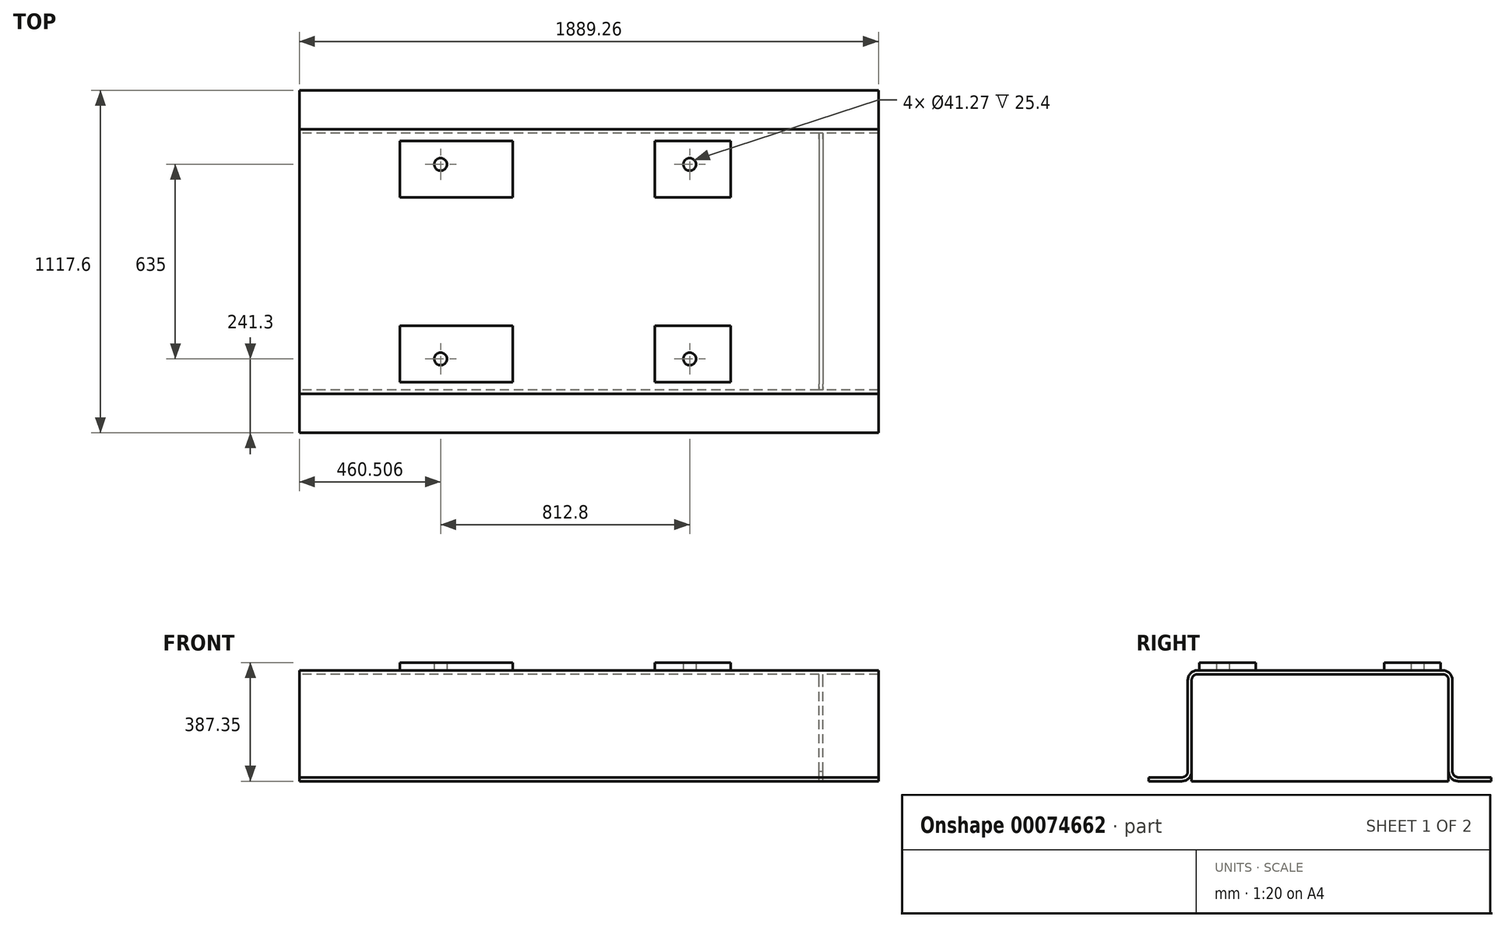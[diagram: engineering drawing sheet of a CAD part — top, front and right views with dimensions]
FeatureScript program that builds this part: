
annotation { "Feature Type Name" : "Feature", "Feature Type Description" : "" }
export const myFeature = defineFeature(function(context is Context, id is Id, definition is map)
    precondition{}
    {
        {
            var Q0;
            Q0=qCreatedBy(makeId("Right.planeOp"),FACE);
            var sketch = newSketch(context, id + "F0", { "sketchPlane" : qUnion([Q0])});
            skLineSegment(sketch, "E0", {"start": v(-558.8, 0) * mm, "end": v(558.8, 0) * mm, "construction": true});
            skLineSegment(sketch, "E1.0", {"start": v(-558.8, 361.95) * mm, "end": v(558.8, 361.95) * mm, "construction": true});
            skLineSegment(sketch, "E2.bottom", {"start": v(0, 361.95) * mm, "end": v(400.05, 361.95) * mm});
            skLineSegment(sketch, "E2.top", {"start": v(450.85, 0) * mm, "end": v(558.8, 0) * mm});
            skLineSegment(sketch, "E2.right", {"start": v(558.8, 12.7) * mm, "end": v(558.8, 0) * mm});
            skLineSegment(sketch, "E3.0", {"start": v(0, 349.25) * mm, "end": v(400.05, 349.25) * mm});
            skLineSegment(sketch, "E4.0", {"start": v(450.85, 12.7) * mm, "end": v(558.8, 12.7) * mm});
            skLineSegment(sketch, "E5", {"start": v(0, -75.24) * mm, "end": v(0, 457.7) * mm, "construction": true});
            skLineSegment(sketch, "E6.0", {"start": v(431.8, 31.75) * mm, "end": v(431.8, 330.2) * mm});
            skLineSegment(sketch, "E7.0", {"start": v(419.1, 31.75) * mm, "end": v(419.1, 330.2) * mm});
            skArc(sketch, "E8.filletArc", {"start": v(419.1, 330.2) * mm, "mid": v(413.52, 343.67) * mm, "end": v(400.05, 349.25) * mm});
            skArc(sketch, "E9.filletArc", {"start": v(431.8, 31.75) * mm, "mid": v(437.38, 18.28) * mm, "end": v(450.85, 12.7) * mm});
            skArc(sketch, "E10.filletArc", {"start": v(431.8, 330.2) * mm, "mid": v(422.5, 352.65) * mm, "end": v(400.05, 361.95) * mm});
            skArc(sketch, "E11.filletArc", {"start": v(419.1, 31.75) * mm, "mid": v(428.4, 9.3) * mm, "end": v(450.85, 0) * mm});
            skLineSegment(sketch, "E12.0", {"start": v(450.85, 6.35) * mm, "end": v(558.8, 6.35) * mm});
            skArc(sketch, "E13.MirrorCS", {"start": v(-419.1, 330.2) * mm, "mid": v(-413.52, 343.67) * mm, "end": v(-400.05, 349.25) * mm});
            skLineSegment(sketch, "E14.MirrorCS", {"start": v(-558.8, 12.7) * mm, "end": v(-558.8, 0) * mm});
            skArc(sketch, "E15.MirrorCS", {"start": v(-431.8, 31.75) * mm, "mid": v(-437.38, 18.28) * mm, "end": v(-450.85, 12.7) * mm});
            skLineSegment(sketch, "E16.MirrorCS", {"start": v(-450.85, 6.35) * mm, "end": v(-558.8, 6.35) * mm});
            skLineSegment(sketch, "E17.MirrorCS", {"start": v(-450.85, 12.7) * mm, "end": v(-558.8, 12.7) * mm});
            skLineSegment(sketch, "E18.MirrorCS", {"start": v(-450.85, 0) * mm, "end": v(-558.8, 0) * mm});
            skArc(sketch, "E19.MirrorCS", {"start": v(-419.1, 31.75) * mm, "mid": v(-428.4, 9.3) * mm, "end": v(-450.85, 0) * mm});
            skArc(sketch, "E20.MirrorCS", {"start": v(-431.8, 330.2) * mm, "mid": v(-422.5, 352.65) * mm, "end": v(-400.05, 361.95) * mm});
            skLineSegment(sketch, "E21.MirrorCS", {"start": v(-431.8, 31.75) * mm, "end": v(-431.8, 330.2) * mm});
            skLineSegment(sketch, "E22.MirrorCS", {"start": v(0, 349.25) * mm, "end": v(-400.05, 349.25) * mm});
            skLineSegment(sketch, "E23.MirrorCS", {"start": v(-419.1, 31.75) * mm, "end": v(-419.1, 330.2) * mm});
            skLineSegment(sketch, "E24.MirrorCS", {"start": v(0, 361.95) * mm, "end": v(-400.05, 361.95) * mm});
            skSolve(sketch);
        }
        {
            var Q0;
            Q0 = qSketchRegion(id + "F0", true);
            extrude(context, id + "F1", {"entities" : qUnion([Q0]), "endBound" : BoundingType.SYMMETRIC, "depth" : 1889.25 * mm});
        }
        {
            var Q0;
            Q0=makeQuery(id+"F1.opExtrude","SWEPT_FACE",FACE,{"disambiguationData":[OSD([sQuery(id+"F0.wireOp",EDGE,"E3.0"),sQuery(id+"F0.wireOp",EDGE,"E22.MirrorCS")])]});
            var sketch = newSketch(context, id + "F2", { "sketchPlane" : qUnion([Q0])});
            skLineSegment(sketch, "E25.0", {"start": v(763.78, 419.1) * mm, "end": v(751.08, 419.1) * mm});
            skLineSegment(sketch, "E26.0", {"start": v(763.78, -419.1) * mm, "end": v(751.08, -419.1) * mm});
            skLineSegment(sketch, "E27.0", {"start": v(763.78, -419.1) * mm, "end": v(763.78, 419.1) * mm});
            skLineSegment(sketch, "E28.0", {"start": v(751.08, -419.1) * mm, "end": v(751.08, 419.1) * mm});
            skPoint(sketch, "E29.orphan", {"position": v(-944.63, 419.1) * mm});
            skPoint(sketch, "E30.orphan", {"position": v(944.63, 419.1) * mm});
            skPoint(sketch, "E31.orphan", {"position": v(944.63, -419.1) * mm});
            skPoint(sketch, "E32.orphan", {"position": v(-944.63, -419.1) * mm});
            skSolve(sketch);
        }
        {
            var Q0;
            Q0 = qSketchRegion(id + "F2", true);
            var Q1;
            Q1=makeQuery(id+"F1.opExtrude","SWEPT_FACE",FACE,{"disambiguationData":[OSD([sQuery(id+"F0.wireOp",EDGE,"E18.MirrorCS")])]});
            extrude(context, id + "F3", {"entities" : qUnion([Q0]), "operationType" : NewBodyOperationType.ADD, "endBound" : BoundingType.UP_TO_SURFACE, "endBoundEntityFace" : qUnion([Q1]), "depth" : 25.4 * mm});
        }
        {
            var Q0;
            Q0=makeQuery(id+"F1.opExtrude","SWEPT_FACE",FACE,{"disambiguationData":[OSD([sQuery(id+"F0.wireOp",EDGE,"E2.bottom"),sQuery(id+"F0.wireOp",EDGE,"E24.MirrorCS")])]});
            var sketch = newSketch(context, id + "F4", { "sketchPlane" : qUnion([Q0])});
            skLineSegment(sketch, "E33.0", {"start": v(-1820.93, -1308.8) * mm, "end": v(-1820.93, -495.23) * mm, "construction": true});
            skLineSegment(sketch, "E34.0", {"start": v(-1319.28, -1308.8) * mm, "end": v(-1319.28, -495.23) * mm, "construction": true});
            skLineSegment(sketch, "E35.0", {"start": v(-77.72, -1308.8) * mm, "end": v(-77.72, 594.77) * mm, "construction": true});
            skLineSegment(sketch, "E36.0", {"start": v(716.03, -1308.8) * mm, "end": v(716.03, -495.23) * mm, "construction": true});
            skLineSegment(sketch, "E37.0", {"start": v(-249.17, -1308.8) * mm, "end": v(-249.17, 594.77) * mm, "construction": true});
            skLineSegment(sketch, "E38.0", {"start": v(-617.47, -1308.8) * mm, "end": v(-617.47, 594.77) * mm, "construction": true});
            skLineSegment(sketch, "E39.0", {"start": v(214.38, -1308.8) * mm, "end": v(214.38, 594.77) * mm, "construction": true});
            skLineSegment(sketch, "E40.0", {"start": v(462.03, -1308.8) * mm, "end": v(462.03, 594.77) * mm, "construction": true});
            skLineSegment(sketch, "E41", {"start": v(-1320.83, 0) * mm, "end": v(1097.9, 0) * mm, "construction": true});
            skLineSegment(sketch, "E42.0", {"start": v(-1320.83, 209.55) * mm, "end": v(1097.9, 209.55) * mm, "construction": true});
            skLineSegment(sketch, "E43.0", {"start": v(-1320.83, 393.7) * mm, "end": v(1097.9, 393.7) * mm, "construction": true});
            skLineSegment(sketch, "E44.bottom", {"start": v(-617.47, 393.7) * mm, "end": v(-249.17, 393.7) * mm});
            skLineSegment(sketch, "E44.top", {"start": v(-617.47, 209.55) * mm, "end": v(-249.17, 209.55) * mm});
            skLineSegment(sketch, "E44.left", {"start": v(-617.47, 393.7) * mm, "end": v(-617.47, 209.55) * mm});
            skLineSegment(sketch, "E44.right", {"start": v(-249.17, 393.7) * mm, "end": v(-249.17, 209.55) * mm});
            skLineSegment(sketch, "E45.bottom", {"start": v(214.38, 209.55) * mm, "end": v(462.03, 209.55) * mm});
            skLineSegment(sketch, "E45.top", {"start": v(214.38, 393.7) * mm, "end": v(462.03, 393.7) * mm});
            skLineSegment(sketch, "E45.left", {"start": v(214.38, 209.55) * mm, "end": v(214.38, 393.7) * mm});
            skLineSegment(sketch, "E45.right", {"start": v(462.03, 209.55) * mm, "end": v(462.03, 393.7) * mm});
            skLineSegment(sketch, "E46.0", {"start": v(-484.12, -1308.8) * mm, "end": v(-484.12, 594.77) * mm, "construction": true});
            skLineSegment(sketch, "E47.0", {"start": v(328.68, -1308.8) * mm, "end": v(328.68, 594.77) * mm, "construction": true});
            skLineSegment(sketch, "E48.0", {"start": v(-1320.83, 317.5) * mm, "end": v(1097.9, 317.5) * mm, "construction": true});
            skCircle(sketch, "E49", {"center": v(-484.12, 317.5) * mm, "radius": 20.64 * mm});
            skCircle(sketch, "E50", {"center": v(328.68, 317.5) * mm, "radius": 20.64 * mm});
            skCircle(sketch, "E51.MirrorC", {"center": v(-484.12, -317.5) * mm, "radius": 20.64 * mm});
            skCircle(sketch, "E52.MirrorC", {"center": v(328.68, -317.5) * mm, "radius": 20.64 * mm});
            skLineSegment(sketch, "E53.MirrorCS", {"start": v(214.38, -393.7) * mm, "end": v(462.03, -393.7) * mm});
            skLineSegment(sketch, "E54.MirrorCS", {"start": v(214.38, -209.55) * mm, "end": v(214.38, -393.7) * mm});
            skLineSegment(sketch, "E55.MirrorCS", {"start": v(462.03, -209.55) * mm, "end": v(462.03, -393.7) * mm});
            skLineSegment(sketch, "E56.MirrorCS", {"start": v(-617.47, -393.7) * mm, "end": v(-617.47, -209.55) * mm});
            skLineSegment(sketch, "E57.MirrorCS", {"start": v(-617.47, -393.7) * mm, "end": v(-249.17, -393.7) * mm});
            skLineSegment(sketch, "E58.MirrorCS", {"start": v(-617.47, -209.55) * mm, "end": v(-249.17, -209.55) * mm});
            skLineSegment(sketch, "E59.MirrorCS", {"start": v(214.38, -209.55) * mm, "end": v(462.03, -209.55) * mm});
            skLineSegment(sketch, "E60.MirrorCS", {"start": v(-249.17, -393.7) * mm, "end": v(-249.17, -209.55) * mm});
            skSolve(sketch);
        }
        {
            var Q0;
            Q0 = qSketchRegion(id + "F4", true);
            extrude(context, id + "F5", {"entities" : qUnion([Q0]), "operationType" : NewBodyOperationType.ADD, "depth" : 25.4 * mm});
        }
    });
